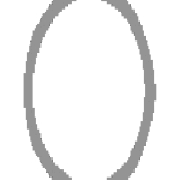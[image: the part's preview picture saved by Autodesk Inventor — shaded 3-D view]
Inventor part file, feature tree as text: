
AUTODESK INVENTOR PART (.ipt)
format: ipt  version: 2021 (Build 250183000, 183)  size: 110,080 bytes
history: native  units: in
note: dims shown in document units (in); Inventor stores cm internally (conversion verified against a paired STEP export)
features: other x4, sketch x3, plane x1
ambient origin geometry x8: Origin, YZ Plane, XZ Plane, XY Plane, X Axis, Y Axis, Z Axis, Center Point
bodies: Solid1 (feature_tree), Body (feature_tree)
feature tree (8):
  other  "Driven Length"
  other  "Frame Generator"
  other  "Start Plane"
  other  "End Plane"
  sketch  "Sketch"  dims[d2=15.625in d4=-0.0in d5=15.625in d6=0.12in d7=0.0in d8=90.0deg d9=15.625in]
  sketch  "Sketch2"  dims[d0=1.0in]
  plane  "Work Plane3"
  sketch  "Sketch3"  dims[d1=0.065in]
